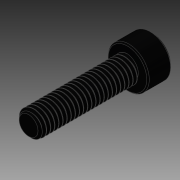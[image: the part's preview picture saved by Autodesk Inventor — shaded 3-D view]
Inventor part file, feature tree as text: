
AUTODESK INVENTOR PART (.ipt)
format: ipt  version: 2014 SP1 (Build 180222100, 222)  size: 658,432 bytes
history: native  units: in
note: dims shown in document units (in); Inventor stores cm internally (conversion verified against a paired STEP export)
features: chamfer x1, other x1, imported_body x1
ambient origin geometry x8: Origin, YZ Plane, XZ Plane, XY Plane, X Axis, Y Axis, Z Axis, Center Point
bodies: Body1 (feature_tree)
feature tree (3):
  chamfer  "Chamfer2"  [1 undecoded]
  other  "91251A3451"
  imported_body  "Base1"
note: 1 required parameter value undecoded (feature->parameter linkage not recoverable at this tier; creation-order binding heuristic only, values carry confidence <= 0.55)
